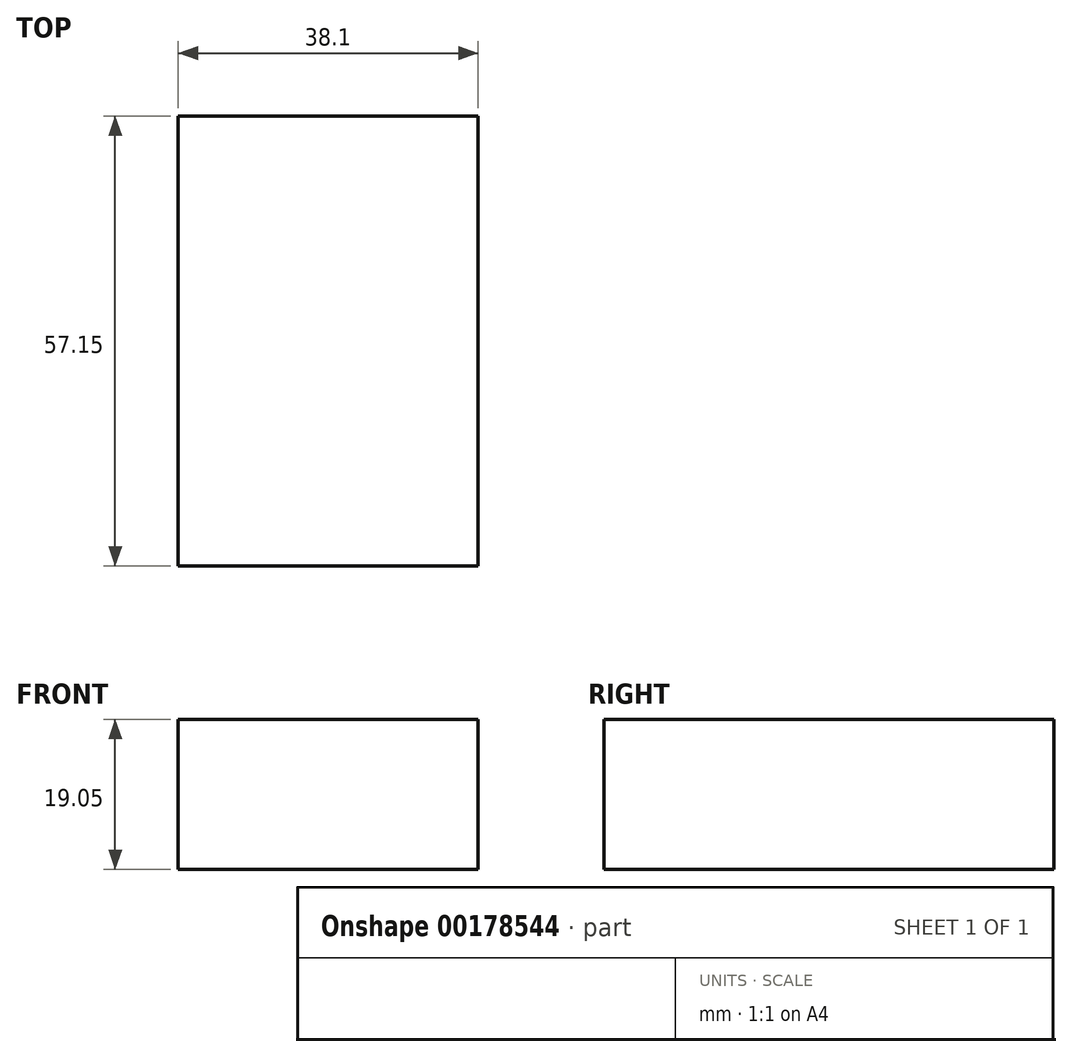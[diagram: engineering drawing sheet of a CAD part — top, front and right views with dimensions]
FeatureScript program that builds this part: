
annotation { "Feature Type Name" : "Feature", "Feature Type Description" : "" }
export const myFeature = defineFeature(function(context is Context, id is Id, definition is map)
    precondition{}
    {
        {
            var Q0;
            Q0=qCreatedBy(makeId("Front.planeOp"),FACE);
            var sketch = newSketch(context, id + "F0", { "sketchPlane" : qUnion([Q0])});
            skLineSegment(sketch, "E0.bottom", {"start": v(-60.78, 0) * mm, "end": v(-41.73, 0) * mm});
            skLineSegment(sketch, "E0.top", {"start": v(-60.78, 19.05) * mm, "end": v(-41.73, 19.05) * mm});
            skLineSegment(sketch, "E0.left", {"start": v(-60.78, 0) * mm, "end": v(-60.78, 19.05) * mm});
            skLineSegment(sketch, "E0.right", {"start": v(-41.73, 0) * mm, "end": v(-41.73, 19.05) * mm});
            skLineSegment(sketch, "E1.bottom", {"start": v(-41.73, 0) * mm, "end": v(-22.68, 0) * mm});
            skLineSegment(sketch, "E1.top", {"start": v(-41.73, 19.05) * mm, "end": v(-22.68, 19.05) * mm});
            skLineSegment(sketch, "E1.right", {"start": v(-22.68, 0) * mm, "end": v(-22.68, 19.05) * mm});
            skSolve(sketch);
        }
        {
            var Q0;
            Q0 = qSketchRegion(id + "F0", true);
            extrude(context, id + "F1", {"entities" : qUnion([Q0]), "oppositeDirection" : true, "depth" : 57.15 * mm});
        }
    });
